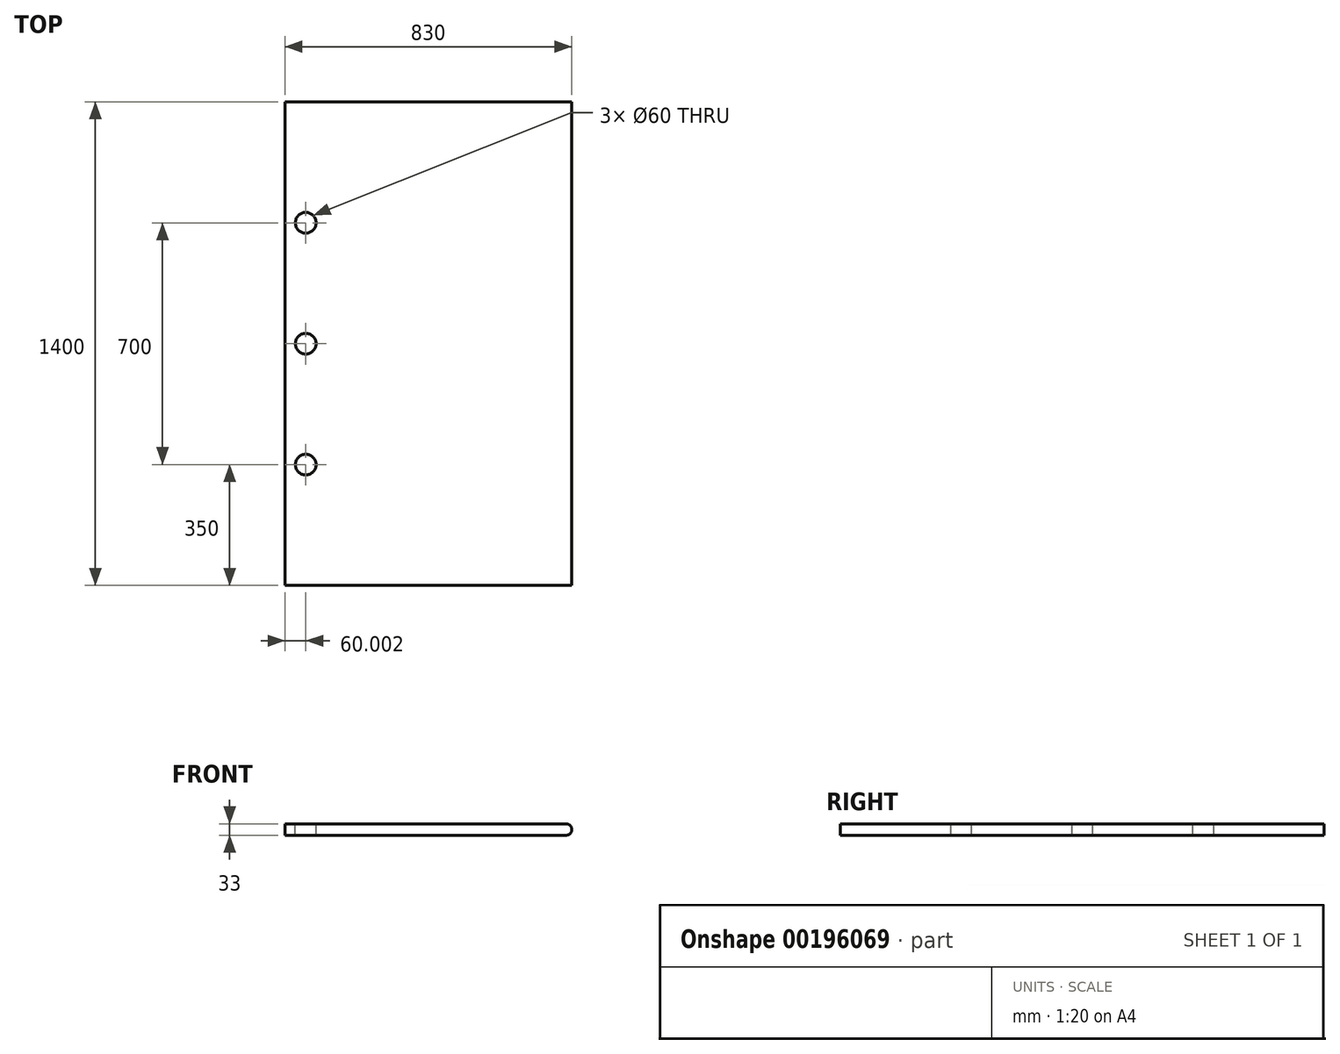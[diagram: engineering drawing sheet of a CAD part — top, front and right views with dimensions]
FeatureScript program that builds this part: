
annotation { "Feature Type Name" : "Feature", "Feature Type Description" : "" }
export const myFeature = defineFeature(function(context is Context, id is Id, definition is map)
    precondition{}
    {
        {
            var Q0;
            Q0=qCreatedBy(makeId("Top.planeOp"),FACE);
            var sketch = newSketch(context, id + "F0", { "sketchPlane" : qUnion([Q0])});
            skLineSegment(sketch, "E0.bottom", {"start": v(-60.53, -1400) * mm, "end": v(769.47, -1400) * mm});
            skLineSegment(sketch, "E0.top", {"start": v(-60.53, 0) * mm, "end": v(769.47, 0) * mm});
            skLineSegment(sketch, "E0.left", {"start": v(-60.53, -1400) * mm, "end": v(-60.53, 0) * mm});
            skLineSegment(sketch, "E0.right", {"start": v(769.47, -1400) * mm, "end": v(769.47, 0) * mm});
            skSolve(sketch);
        }
        {
            var Q0;
            Q0=makeQuery(id+"F0.imprint","IMPRINT",FACE,{"disambiguationData":[TD([[makeQuery(id+"F0.imprint","IMPRINT",EDGE,{"derivedFrom":sQuery(id+"F0.wireOp",EDGE,"E0.bottom")}),1.0]])]});
            extrude(context, id + "F1", {"entities" : qUnion([Q0]), "depth" : 33 * mm});
        }
        {
            var Q0;
            Q0=makeQuery(id+"F1.opExtrude","CAP_EDGE",EDGE,{"disambiguationData":[OSD([sQuery(id+"F0.wireOp",EDGE,"E0.right")])],"isStart":false});
            var Q1;
            Q1=makeQuery(id+"F1.opExtrude","CAP_EDGE",EDGE,{"disambiguationData":[OSD([sQuery(id+"F0.wireOp",EDGE,"E0.right")])],"isStart":true});
            fillet(context, id + "F2", {"entities" : qUnion([Q0, Q1]), "radius" : 16.5 * mm, "tangentPropagation" : true, "allowEdgeOverflow" : false});
        }
        {
            var Q0;
            Q0=makeQuery(id+"F1.opExtrude","CAP_FACE",FACE,{"disambiguationData":[OSD([sQuery(id+"F0.wireOp",EDGE,"E0.bottom"),sQuery(id+"F0.wireOp",EDGE,"E0.top"),sQuery(id+"F0.wireOp",EDGE,"E0.left"),sQuery(id+"F0.wireOp",EDGE,"E0.right")])],"isStart":false});
            var sketch = newSketch(context, id + "F3", { "sketchPlane" : qUnion([Q0])});
            skPoint(sketch, "E1", {"position": v(-0.53, -1050) * mm});
            skPoint(sketch, "E2", {"position": v(-0.53, -700) * mm});
            skPoint(sketch, "E3", {"position": v(-0.53, -350) * mm});
            skLineSegment(sketch, "E4", {"start": v(-0.53, -350) * mm, "end": v(-0.53, -1050) * mm});
            skSolve(sketch);
        }
        {
            var Q0;
            Q0=sQuery(id+"F3.wireOp",VERTEX,"E1");
            var Q1;
            Q1=sQuery(id+"F3.wireOp",VERTEX,"E2");
            var Q2;
            Q2=sQuery(id+"F3.wireOp",VERTEX,"E3");
            var Q3;
            Q3=makeQuery(id+"F1.opExtrude","SWEPT_BODY",BODY,{"disambiguationData":[OSD([sQuery(id+"F0.wireOp",EDGE,"E0.bottom"),sQuery(id+"F0.wireOp",EDGE,"E0.top"),sQuery(id+"F0.wireOp",EDGE,"E0.left"),sQuery(id+"F0.wireOp",EDGE,"E0.right")])]});
            hole(context, id + "F4", {"style" : HoleStyle.SIMPLE, "endStyle" : HoleEndStyle.THROUGH, "holeDiameter" : 60 * mm, "locations" : qUnion([Q0, Q1, Q2]), "scope" : qUnion([Q3]), "isTappedThrough" : true});
        }
    });
